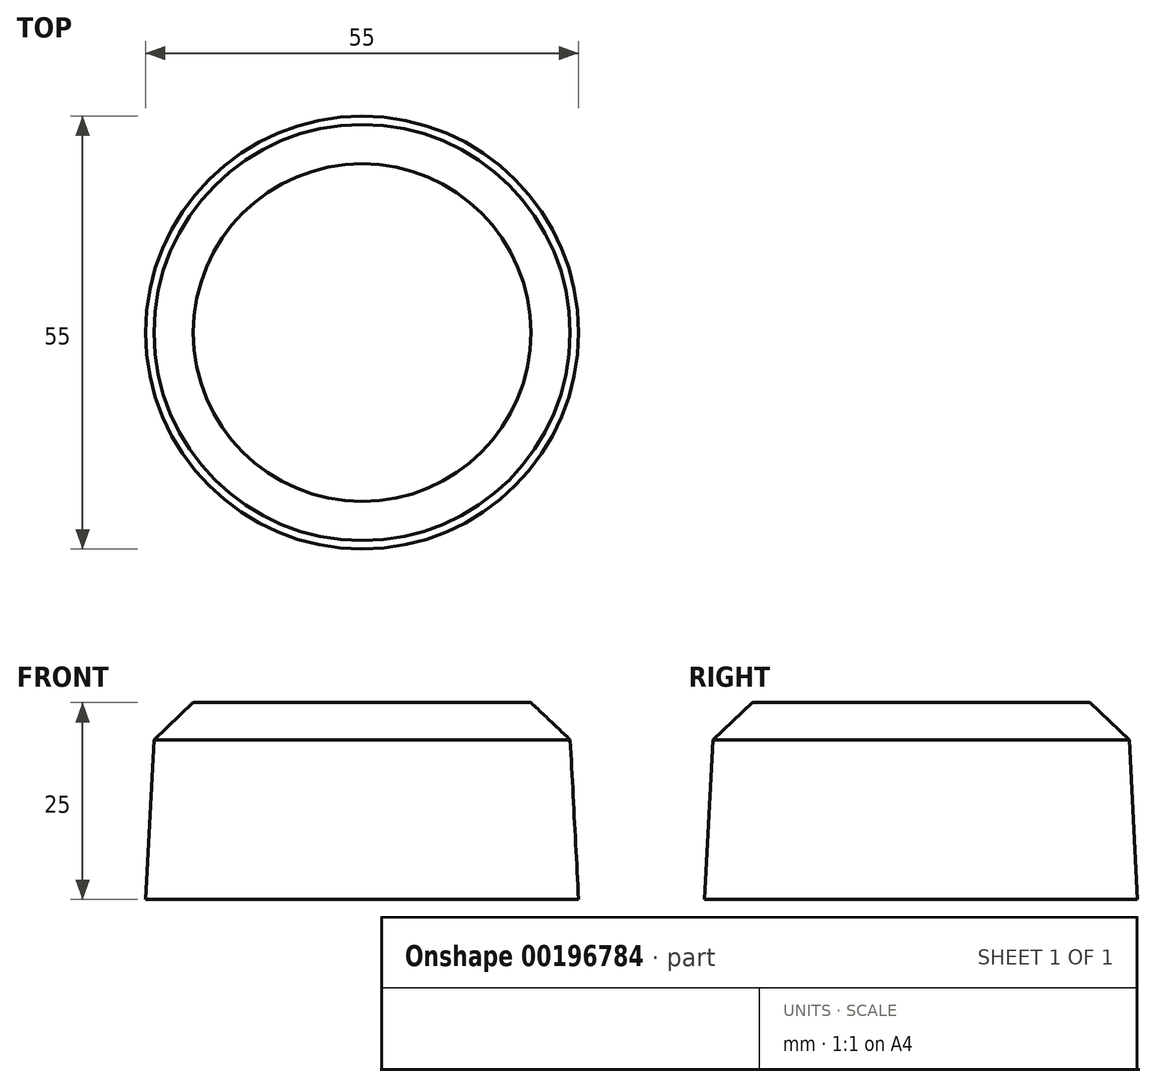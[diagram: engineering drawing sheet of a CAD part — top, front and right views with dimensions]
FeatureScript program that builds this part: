
annotation { "Feature Type Name" : "Feature", "Feature Type Description" : "" }
export const myFeature = defineFeature(function(context is Context, id is Id, definition is map)
    precondition{}
    {
        {
            var Q0;
            Q0=qCreatedBy(makeId("Top.planeOp"),FACE);
            var sketch = newSketch(context, id + "F0", { "sketchPlane" : qUnion([Q0])});
            skCircle(sketch, "E0", {"center": v(0, 0) * mm, "radius": 27.5 * mm});
            skSolve(sketch);
        }
        {
            var Q0;
            Q0 = qSketchRegion(id + "F0", true);
            extrude(context, id + "F1", {"entities" : qUnion([Q0]), "depth" : 25 * mm, "hasDraft" : true, "draftAngle" : 3 * degree, "draftPullDirection" : true});
        }
        {
            var Q0;
            Q0=makeQuery(id+"F1.opExtrude","CAP_EDGE",EDGE,{"disambiguationData":[OSD([sQuery(id+"F0.wireOp",EDGE,"E0")])],"isStart":false});
            chamfer(context, id + "F2", {"entities" : qUnion([Q0]), "width" : 5 * mm, "tangentPropagation" : true});
        }
    });
